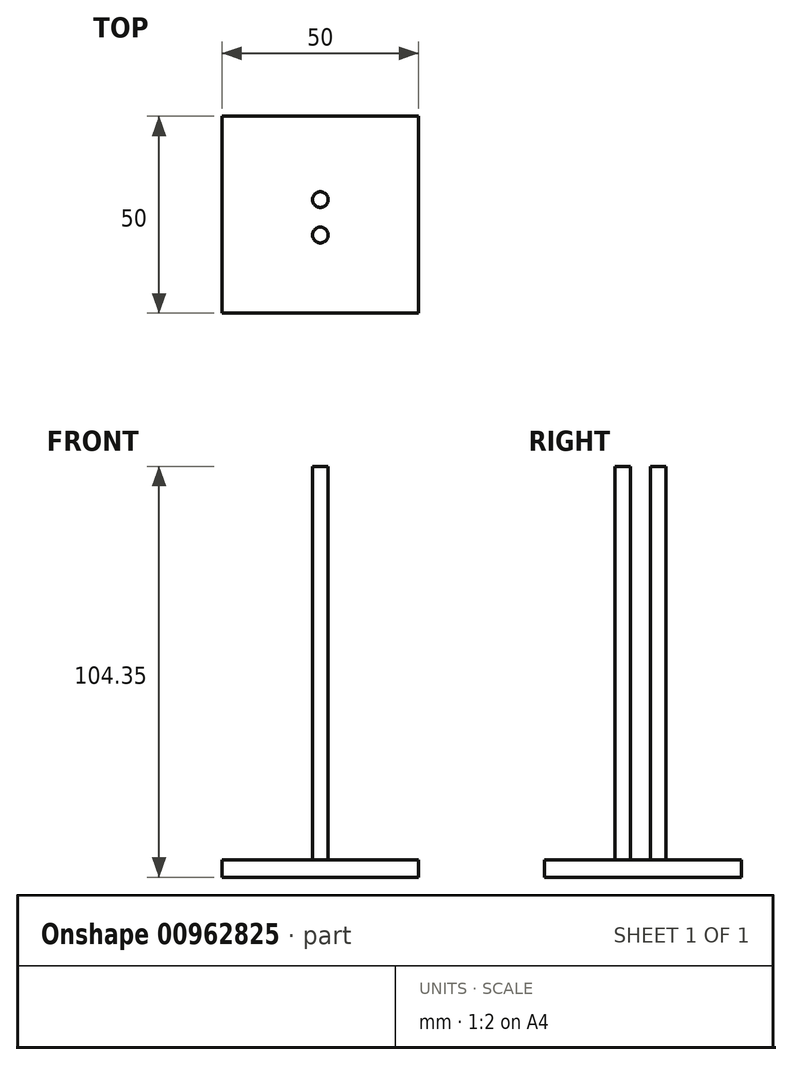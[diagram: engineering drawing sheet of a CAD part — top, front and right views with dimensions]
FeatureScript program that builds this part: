
annotation { "Feature Type Name" : "Feature", "Feature Type Description" : "" }
export const myFeature = defineFeature(function(context is Context, id is Id, definition is map)
    precondition{}
    {
        {
            var Q0;
            Q0=qCreatedBy(makeId("Top.planeOp"),FACE);
            var sketch = newSketch(context, id + "F0", { "sketchPlane" : qUnion([Q0])});
            skLineSegment(sketch, "E0.bottom", {"start": v(25, 25) * mm, "end": v(-25, 25) * mm});
            skLineSegment(sketch, "E0.top", {"start": v(25, -25) * mm, "end": v(-25, -25) * mm});
            skLineSegment(sketch, "E0.left", {"start": v(25, 25) * mm, "end": v(25, -25) * mm});
            skLineSegment(sketch, "E0.right", {"start": v(-25, 25) * mm, "end": v(-25, -25) * mm});
            skPoint(sketch, "E0.middle", {"position": v(0, 0) * mm});
            skSolve(sketch);
        }
        {
            var Q0;
            Q0 = qSketchRegion(id + "F0", true);
            extrude(context, id + "F1", {"entities" : qUnion([Q0]), "depth" : 4.35 * mm, "offsetDistance" : 25 * mm});
        }
        {
            var Q0;
            Q0=makeQuery(id+"F1.opExtrude","CAP_FACE",FACE,{"disambiguationData":[OSD([sQuery(id+"F0.wireOp",EDGE,"E0.bottom"),sQuery(id+"F0.wireOp",EDGE,"E0.top"),sQuery(id+"F0.wireOp",EDGE,"E0.left"),sQuery(id+"F0.wireOp",EDGE,"E0.right")])],"isStart":false});
            var sketch = newSketch(context, id + "F2", { "sketchPlane" : qUnion([Q0])});
            skCircle(sketch, "E1", {"center": v(0, 3.82) * mm, "radius": 2 * mm});
            skCircle(sketch, "E2", {"center": v(0, -5.18) * mm, "radius": 2 * mm});
            skSolve(sketch);
        }
        {
            var Q0;
            Q0=makeQuery(id+"F2.imprint","IMPRINT",FACE,{"disambiguationData":[TD([[makeQuery(id+"F2.imprint","IMPRINT",EDGE,{"derivedFrom":sQuery(id+"F2.wireOp",EDGE,"E2")}),1.0]])]});
            var Q1;
            Q1=makeQuery(id+"F2.imprint","IMPRINT",FACE,{"disambiguationData":[TD([[makeQuery(id+"F2.imprint","IMPRINT",EDGE,{"derivedFrom":sQuery(id+"F2.wireOp",EDGE,"E1")}),1.0]])]});
            extrude(context, id + "F3", {"entities" : qUnion([Q0, Q1]), "operationType" : NewBodyOperationType.ADD, "depth" : 100 * mm, "offsetDistance" : 25 * mm});
        }
    });
